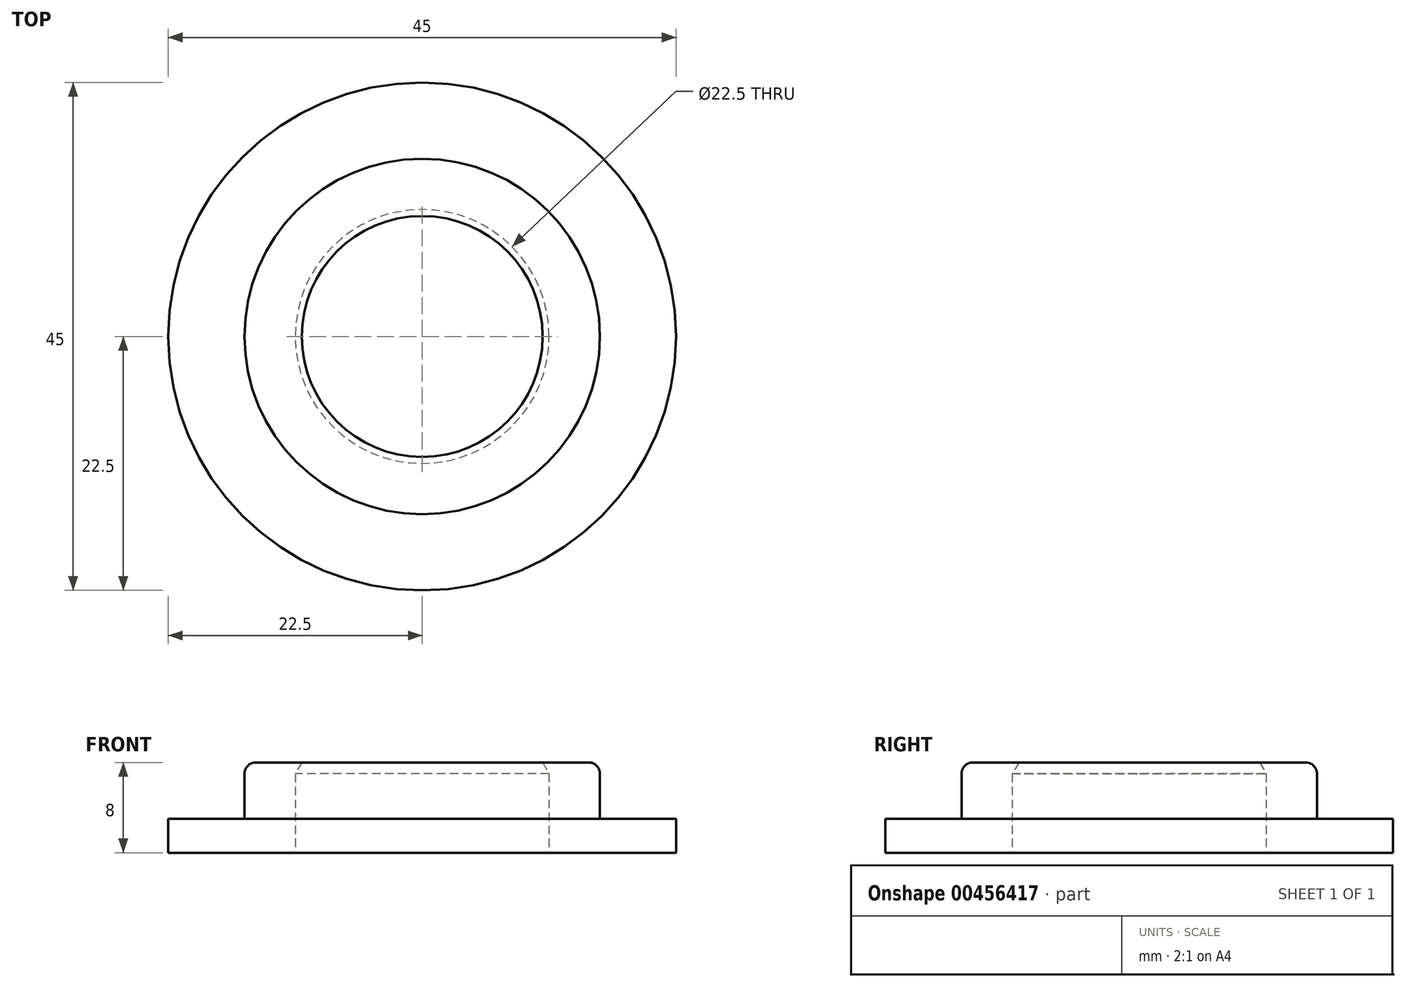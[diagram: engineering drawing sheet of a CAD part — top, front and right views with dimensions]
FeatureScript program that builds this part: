
annotation { "Feature Type Name" : "Feature", "Feature Type Description" : "" }
export const myFeature = defineFeature(function(context is Context, id is Id, definition is map)
    precondition{}
    {
        {
            var Q0;
            Q0=qCreatedBy(makeId("Top.planeOp"),FACE);
            var sketch = newSketch(context, id + "F0", { "sketchPlane" : qUnion([Q0])});
            skCircle(sketch, "E0", {"center": v(0, 0) * mm, "radius": 11.25 * mm});
            skCircle(sketch, "E1", {"center": v(0, 0) * mm, "radius": 15.75 * mm});
            skSolve(sketch);
        }
        {
            var Q0;
            Q0 = qSketchRegion(id + "F0", true);
            extrude(context, id + "F1", {"entities" : qUnion([Q0]), "depth" : 5 * mm});
        }
        {
            var Q0;
            Q0=makeQuery(id+"F1.opExtrude","CAP_FACE",FACE,{"disambiguationData":[OSD([sQuery(id+"F0.wireOp",EDGE,"E0"),sQuery(id+"F0.wireOp",EDGE,"E1")])],"isStart":true});
            var sketch = newSketch(context, id + "F2", { "sketchPlane" : qUnion([Q0])});
            skCircle(sketch, "E2", {"center": v(0, 0) * mm, "radius": 22.5 * mm});
            skCircle(sketch, "E3.0", {"center": v(0, 0) * mm, "radius": 11.25 * mm});
            skSolve(sketch);
        }
        {
            var Q0;
            Q0 = qSketchRegion(id + "F2", true);
            extrude(context, id + "F3", {"entities" : qUnion([Q0]), "operationType" : NewBodyOperationType.ADD, "depth" : 3 * mm});
        }
        {
            var Q0;
            Q0=makeQuery(id+"F1.opExtrude","CAP_FACE",FACE,{"disambiguationData":[OSD([sQuery(id+"F0.wireOp",EDGE,"E0"),sQuery(id+"F0.wireOp",EDGE,"E1")])],"isStart":false});
            var sketch = newSketch(context, id + "F4", { "sketchPlane" : qUnion([Q0])});
            skCircle(sketch, "E4.0", {"center": v(0, 0) * mm, "radius": 11.25 * mm});
            skCircle(sketch, "E5.0", {"center": v(0, 0) * mm, "radius": 10.25 * mm});
            skSolve(sketch);
        }
        {
            var Q0;
            Q0 = qSketchRegion(id + "F4", true);
            extrude(context, id + "F5", {"entities" : qUnion([Q0]), "operationType" : NewBodyOperationType.ADD, "oppositeDirection" : true, "depth" : 1 * mm});
        }
        {
            var Q0;
            Q0=makeQuery(id+"F5.opExtrude","CAP_EDGE",EDGE,{"disambiguationData":[OSD([sQuery(id+"F4.wireOp",EDGE,"E5.0")])],"isStart":false});
            chamfer(context, id + "F6", {"entities" : qUnion([Q0]), "chamferType" : ChamferType.OFFSET_ANGLE, "width" : 1 * mm, "oppositeDirection" : false, "angle" : 60 * degree, "tangentPropagation" : true});
        }
        {
            var Q0;
            Q0=makeQuery(id+"F1.opExtrude","CAP_EDGE",EDGE,{"disambiguationData":[OSD([sQuery(id+"F0.wireOp",EDGE,"E1")])],"isStart":false});
            fillet(context, id + "F7", {"entities" : qUnion([Q0]), "radius" : 1 * mm, "tangentPropagation" : true, "allowEdgeOverflow" : false});
        }
    });
